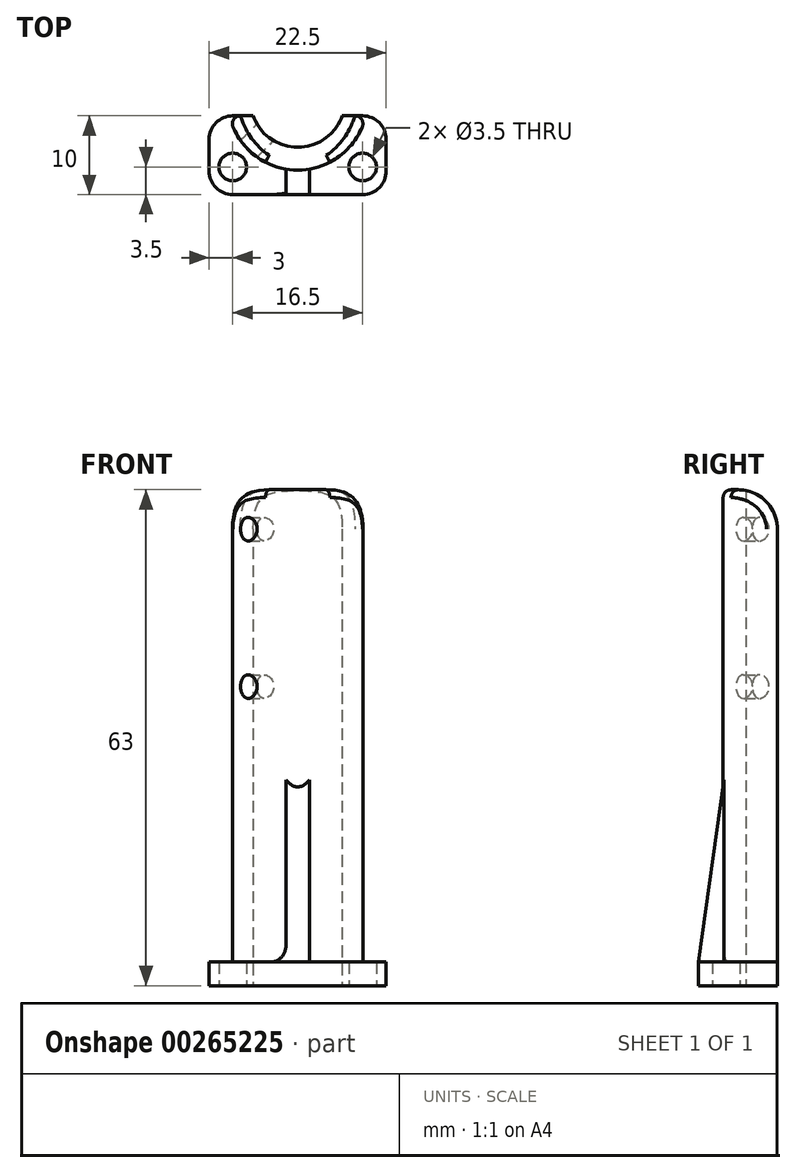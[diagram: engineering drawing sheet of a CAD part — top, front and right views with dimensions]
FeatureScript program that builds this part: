
annotation { "Feature Type Name" : "Feature", "Feature Type Description" : "" }
export const myFeature = defineFeature(function(context is Context, id is Id, definition is map)
    precondition{}
    {
        {
            var Q0;
            Q0=qCreatedBy(makeId("Top.planeOp"),FACE);
            var sketch = newSketch(context, id + "F0", { "sketchPlane" : qUnion([Q0])});
            skLineSegment(sketch, "E0", {"start": v(0, 0) * mm, "end": v(0, 18.16) * mm, "construction": true});
            skLineSegment(sketch, "E1", {"start": v(11.25, 0) * mm, "end": v(-11.25, 0) * mm});
            skLineSegment(sketch, "E2", {"start": v(-11.25, 0) * mm, "end": v(-11.25, 10) * mm});
            skLineSegment(sketch, "E3", {"start": v(-11.25, 10) * mm, "end": v(-8.25, 10) * mm});
            skLineSegment(sketch, "E4", {"start": v(11.25, 10) * mm, "end": v(11.25, 0) * mm});
            skLineSegment(sketch, "E5", {"start": v(-8.25, 0) * mm, "end": v(-8.25, 10) * mm, "construction": true});
            skLineSegment(sketch, "E6", {"start": v(8.25, 0) * mm, "end": v(8.25, 10) * mm, "construction": true});
            skCircle(sketch, "E7", {"center": v(-8.25, 3.5) * mm, "radius": 1.75 * mm});
            skCircle(sketch, "E8", {"center": v(8.25, 3.5) * mm, "radius": 1.75 * mm});
            skLineSegment(sketch, "E9", {"start": v(-8.25, 3.5) * mm, "end": v(8.25, 3.5) * mm, "construction": true});
            skCircle(sketch, "E10", {"center": v(0, 12) * mm, "radius": 6 * mm, "construction": true});
            skPoint(sketch, "E11.orphan", {"position": v(-5.25, 0) * mm});
            skArc(sketch, "E12", {"start": v(-5.66, 10) * mm, "mid": v(0, 6) * mm, "end": v(5.66, 10) * mm});
            skLineSegment(sketch, "E13.trimOffspring", {"start": v(5.66, 10) * mm, "end": v(11.25, 10) * mm});
            skLineSegment(sketch, "E14", {"start": v(-8.25, 10) * mm, "end": v(-5.66, 10) * mm});
            skSolve(sketch);
        }
        {
            var Q0;
            Q0 = qSketchRegion(id + "F0", true);
            extrude(context, id + "F1", {"entities" : qUnion([Q0]), "depth" : 3 * mm});
        }
        {
            var Q0;
            Q0=makeQuery(id+"F1.opExtrude","CAP_FACE",FACE,{"disambiguationData":[OSD([sQuery(id+"F0.wireOp",EDGE,"As0BfuVP-EvKX-IIzB-8RFU-CAgbb2jAcoWc"),sQuery(id+"F0.wireOp",EDGE,"L4OFp0fu-src7-8fQ3-r4xW-09PvagWeFecp"),sQuery(id+"F0.wireOp",EDGE,"D5aVDjwy-oaWC-XehB-VUHR-Bb3EUq3Xvnb7"),sQuery(id+"F0.wireOp",EDGE,"E1"),sQuery(id+"F0.wireOp",EDGE,"E2"),sQuery(id+"F0.wireOp",EDGE,"E3"),sQuery(id+"F0.wireOp",EDGE,"E4"),sQuery(id+"F0.wireOp",EDGE,"Iq0820Bf-KlZ2-tIK3-RNVn-SmXuxhuQHUvB"),sQuery(id+"F0.wireOp",EDGE,"E7"),sQuery(id+"F0.wireOp",EDGE,"E8")])],"isStart":false});
            var sketch = newSketch(context, id + "F2", { "sketchPlane" : qUnion([Q0])});
            skArc(sketch, "E15.0", {"start": v(-5.66, 10) * mm, "mid": v(0, 6) * mm, "end": v(5.66, 10) * mm});
            skLineSegment(sketch, "E16", {"start": v(-5.66, 10) * mm, "end": v(-8.66, 10) * mm});
            skLineSegment(sketch, "E17", {"start": v(5.66, 10) * mm, "end": v(8.66, 10) * mm});
            skArc(sketch, "E18", {"start": v(-8.66, 10) * mm, "mid": v(0, 3.12) * mm, "end": v(8.66, 10) * mm});
            skSolve(sketch);
        }
        {
            var Q0;
            Q0 = qSketchRegion(id + "F2", true);
            extrude(context, id + "F3", {"entities" : qUnion([Q0]), "operationType" : NewBodyOperationType.ADD, "depth" : 60 * mm});
        }
        {
            var Q0;
            Q0=makeQuery(id+"F1.opExtrude","CAP_FACE",FACE,{"disambiguationData":[OSD([sQuery(id+"F0.wireOp",EDGE,"E1"),sQuery(id+"F0.wireOp",EDGE,"E2"),sQuery(id+"F0.wireOp",EDGE,"E3"),sQuery(id+"F0.wireOp",EDGE,"E4"),sQuery(id+"F0.wireOp",EDGE,"E7"),sQuery(id+"F0.wireOp",EDGE,"E8"),sQuery(id+"F0.wireOp",EDGE,"E12"),sQuery(id+"F0.wireOp",EDGE,"E13.trimOffspring"),sQuery(id+"F0.wireOp",EDGE,"E14")])],"isStart":false});
            var sketch = newSketch(context, id + "F4", { "sketchPlane" : qUnion([Q0])});
            skLineSegment(sketch, "E19", {"start": v(0, 0) * mm, "end": v(0, 3.12) * mm, "construction": true});
            skLineSegment(sketch, "E20", {"start": v(0, 0) * mm, "end": v(1.5, 0) * mm});
            skLineSegment(sketch, "E21", {"start": v(1.5, 0) * mm, "end": v(1.5, 3.24) * mm});
            skLineSegment(sketch, "E22", {"start": v(0, 0) * mm, "end": v(-1.5, 0) * mm});
            skLineSegment(sketch, "E23", {"start": v(-1.5, 0) * mm, "end": v(-1.5, 3.24) * mm});
            skArc(sketch, "E24.0", {"start": v(-1.5, 3.24) * mm, "mid": v(0, 3.12) * mm, "end": v(1.5, 3.24) * mm});
            skPoint(sketch, "E25.orphan", {"position": v(-8.66, 10) * mm});
            skPoint(sketch, "E26.orphan", {"position": v(8.66, 10) * mm});
            skSolve(sketch);
        }
        {
            var Q0;
            Q0 = qSketchRegion(id + "F4", true);
            extrude(context, id + "F5", {"entities" : qUnion([Q0]), "operationType" : NewBodyOperationType.ADD, "depth" : 25 * mm});
        }
        {
            var Q0;
            Q0=makeQuery(id+"F5.opExtrude","CAP_EDGE",EDGE,{"disambiguationData":[OSD([sQuery(id+"F4.wireOp",EDGE,"E20"),sQuery(id+"F4.wireOp",EDGE,"E22")])],"isStart":false});
            chamfer(context, id + "F6", {"entities" : qUnion([Q0]), "chamferType" : ChamferType.TWO_OFFSETS, "width1" : 25 * mm, "oppositeDirection" : false, "width2" : 3.5 * mm, "tangentPropagation" : true});
        }
        {
            var Q0;
            Q0=makeQuery(id+"F3.opExtrude","CAP_EDGE",EDGE,{"disambiguationData":[OSD([sQuery(id+"F2.wireOp",EDGE,"E17")])],"isStart":false});
            fillet(context, id + "F7", {"entities" : qUnion([Q0]), "radius" : 5 * mm, "tangentPropagation" : true, "allowEdgeOverflow" : false});
        }
        {
            var Q0;
            Q0=makeQuery(id+"F5.opExtrude","CAP_EDGE",EDGE,{"disambiguationData":[OSD([sQuery(id+"F4.wireOp",EDGE,"E21")])],"isStart":true});
            var Q1;
            Q1=makeQuery(id+"F5.opExtrude","CAP_EDGE",EDGE,{"disambiguationData":[OSD([sQuery(id+"F4.wireOp",EDGE,"E23")])],"isStart":true});
            fillet(context, id + "F8", {"entities" : qUnion([Q0, Q1]), "radius" : 2 * mm, "tangentPropagation" : true, "allowEdgeOverflow" : false});
        }
        {
            var Q0;
            Q0=makeQuery(id+"F1.opExtrude","SWEPT_EDGE",EDGE,{"disambiguationData":[OSD([sQuery(id+"F0.wireOp",EDGE,"E1"),sQuery(id+"F0.wireOp",EDGE,"E2")])]});
            var Q1;
            Q1=makeQuery(id+"F1.opExtrude","SWEPT_EDGE",EDGE,{"disambiguationData":[OSD([sQuery(id+"F0.wireOp",EDGE,"E1"),sQuery(id+"F0.wireOp",EDGE,"E4")])]});
            var Q2;
            Q2=makeQuery(id+"F1.opExtrude","SWEPT_EDGE",EDGE,{"disambiguationData":[OSD([sQuery(id+"F0.wireOp",EDGE,"E4"),sQuery(id+"F0.wireOp",EDGE,"E13.trimOffspring")])]});
            var Q3;
            Q3=makeQuery(id+"F1.opExtrude","SWEPT_EDGE",EDGE,{"disambiguationData":[OSD([sQuery(id+"F0.wireOp",EDGE,"E2"),sQuery(id+"F0.wireOp",EDGE,"E3")])]});
            fillet(context, id + "F9", {"entities" : qUnion([Q0, Q1, Q2, Q3]), "radius" : 3 * mm, "tangentPropagation" : true, "allowEdgeOverflow" : false});
        }
        {
            var Q0;
            Q0=makeQuery(id+"F3.opExtrude","CAP_EDGE",EDGE,{"disambiguationData":[OSD([sQuery(id+"F2.wireOp",EDGE,"E18")])],"isStart":false});
            fillet(context, id + "F10", {"entities" : qUnion([Q0]), "radius" : 1 * mm, "tangentPropagation" : true, "allowEdgeOverflow" : false});
        }
        {
            var Q0;
            Q0=qCreatedBy(makeId("Top.planeOp"),FACE);
            var sketch = newSketch(context, id + "F11", { "sketchPlane" : qUnion([Q0])});
            skArc(sketch, "E27.0", {"start": v(-5.66, 10) * mm, "mid": v(0, 6) * mm, "end": v(5.66, 10) * mm, "construction": true});
            skLineSegment(sketch, "E28", {"start": v(0, 12) * mm, "end": v(4.24, 7.76) * mm, "construction": true});
            skLineSegment(sketch, "E29", {"start": v(4.24, 7.76) * mm, "end": v(0, 12) * mm, "construction": true});
            skLineSegment(sketch, "E30", {"start": v(0, 12) * mm, "end": v(-4.24, 7.76) * mm, "construction": true});
            skLineSegment(sketch, "E31", {"start": v(0, 12) * mm, "end": v(0, 8.53) * mm, "construction": true});
            skSolve(sketch);
        }
        {
            var Q0;
            Q0=sQuery(id+"F11.wireOp",EDGE,"E30");
            var Q1;
            Q1=qCreatedBy(makeId("Front.planeOp"),FACE);
            cPlane(context, id + "F12", {"entities" : qUnion([Q0, Q1]), "cplaneType" : CPlaneType.LINE_ANGLE, "offset" : 25 * mm, "angle" : 0 * degree, "width" : 150 * mm, "height" : 150 * mm});
        }
        {
            var Q0;
            Q0=sQuery(id+"F11.wireOp",EDGE,"E29");
            var Q1;
            Q1=qCreatedBy(makeId("Front.planeOp"),FACE);
            cPlane(context, id + "F13", {"entities" : qUnion([Q0, Q1]), "cplaneType" : CPlaneType.LINE_ANGLE, "offset" : 25 * mm, "angle" : 0 * degree, "width" : 150 * mm, "height" : 150 * mm});
        }
        {
            var Q0;
            Q0=qCreatedBy(id+"F13.planeOp",FACE);
            var sketch = newSketch(context, id + "F14", { "sketchPlane" : qUnion([Q0])});
            skPoint(sketch, "E32.0", {"position": v(8.49, 0) * mm});
            skLineSegment(sketch, "E33", {"start": v(8.49, 0) * mm, "end": v(8.49, 58) * mm, "construction": true});
            skCircle(sketch, "E34", {"center": v(8.49, 58) * mm, "radius": 1.5 * mm});
            skCircle(sketch, "E35", {"center": v(8.49, 38) * mm, "radius": 1.5 * mm});
            skSolve(sketch);
        }
        {
            var Q0;
            Q0 = qSketchRegion(id + "F14", true);
            extrude(context, id + "F15", {"entities" : qUnion([Q0]), "operationType" : NewBodyOperationType.REMOVE, "endBound" : BoundingType.THROUGH_ALL, "oppositeDirection" : true, "depth" : 25 * mm});
        }
        {
            var Q0;
            Q0=qCreatedBy(id+"F12.planeOp",FACE);
            var sketch = newSketch(context, id + "F16", { "sketchPlane" : qUnion([Q0])});
            skPoint(sketch, "E36.0", {"position": v(-8.49, 0) * mm});
            skLineSegment(sketch, "E37", {"start": v(-8.49, 0) * mm, "end": v(-8.49, 38.07) * mm, "construction": true});
            skSolve(sketch);
        }
    });
